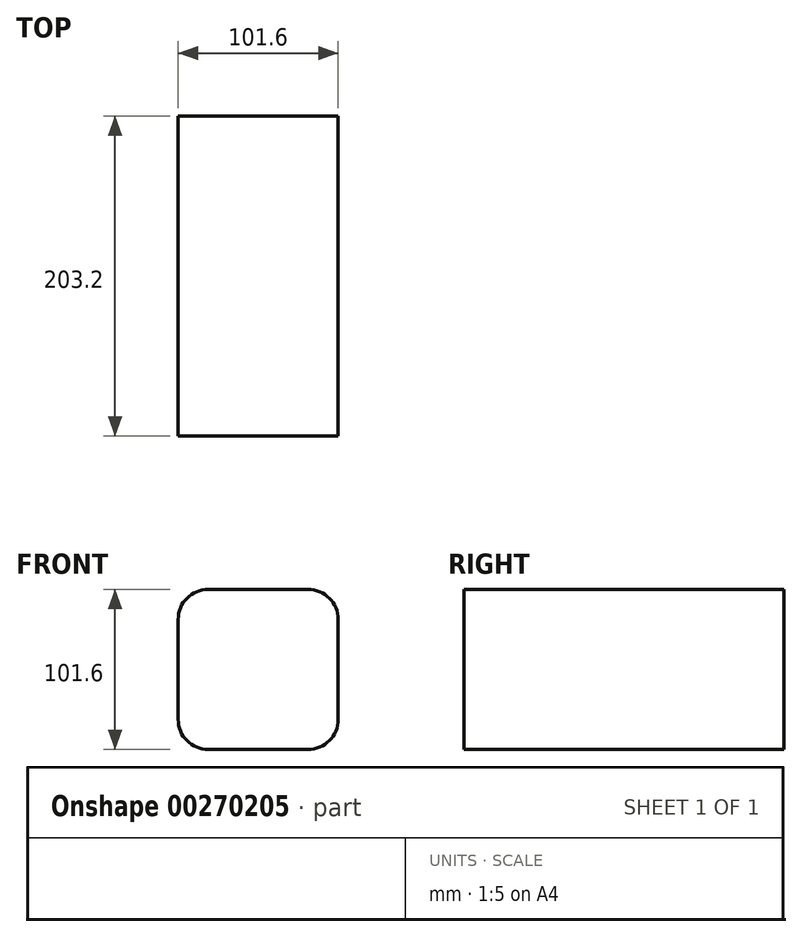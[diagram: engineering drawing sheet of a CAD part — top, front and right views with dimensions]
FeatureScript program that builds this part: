
annotation { "Feature Type Name" : "Feature", "Feature Type Description" : "" }
export const myFeature = defineFeature(function(context is Context, id is Id, definition is map)
    precondition{}
    {
        {
            var Q0;
            Q0=qCreatedBy(makeId("Front.planeOp"),FACE);
            var sketch = newSketch(context, id + "F0", { "sketchPlane" : qUnion([Q0])});
            skLineSegment(sketch, "E0.bottom", {"start": v(50.8, 50.8) * mm, "end": v(-50.8, 50.8) * mm});
            skLineSegment(sketch, "E0.top", {"start": v(50.8, -50.8) * mm, "end": v(-50.8, -50.8) * mm});
            skLineSegment(sketch, "E0.left", {"start": v(50.8, 50.8) * mm, "end": v(50.8, -50.8) * mm});
            skLineSegment(sketch, "E0.right", {"start": v(-50.8, 50.8) * mm, "end": v(-50.8, -50.8) * mm});
            skPoint(sketch, "E0.middle", {"position": v(0, 0) * mm});
            skSolve(sketch);
        }
        {
            var Q0;
            Q0=makeQuery(id+"F0.imprint","IMPRINT",FACE,{"disambiguationData":[TD([[makeQuery(id+"F0.imprint","IMPRINT",EDGE,{"derivedFrom":sQuery(id+"F0.wireOp",EDGE,"E0.bottom")}),1.0]])]});
            extrude(context, id + "F1", {"entities" : qUnion([Q0]), "depth" : 101.6 * mm, "hasSecondDirection" : true, "secondDirectionOppositeDirection" : true, "secondDirectionDepth" : 101.6 * mm});
        }
        {
            var Q0;
            Q0=makeQuery(id+"F1.opExtrude","SWEPT_EDGE",EDGE,{"disambiguationData":[OSD([sQuery(id+"F0.wireOp",EDGE,"E0.bottom"),sQuery(id+"F0.wireOp",EDGE,"E0.right")])]});
            var Q1;
            Q1=makeQuery(id+"F1.opExtrude","SWEPT_EDGE",EDGE,{"disambiguationData":[OSD([sQuery(id+"F0.wireOp",EDGE,"E0.bottom"),sQuery(id+"F0.wireOp",EDGE,"E0.left")])]});
            var Q2;
            Q2=makeQuery(id+"F1.opExtrude","SWEPT_EDGE",EDGE,{"disambiguationData":[OSD([sQuery(id+"F0.wireOp",EDGE,"E0.top"),sQuery(id+"F0.wireOp",EDGE,"E0.left")])]});
            var Q3;
            Q3=makeQuery(id+"F1.opExtrude","SWEPT_EDGE",EDGE,{"disambiguationData":[OSD([sQuery(id+"F0.wireOp",EDGE,"E0.top"),sQuery(id+"F0.wireOp",EDGE,"E0.right")])]});
            fillet(context, id + "F2", {"entities" : qUnion([Q0, Q1, Q2, Q3]), "radius" : 19.05 * mm, "tangentPropagation" : true, "allowEdgeOverflow" : false});
        }
        {
            var Q0;
            Q0=makeQuery(id+"F1.opExtrude","SWEPT_FACE",FACE,{"disambiguationData":[OSD([sQuery(id+"F0.wireOp",EDGE,"E0.top")])]});
            var sketch = newSketch(context, id + "F3", { "sketchPlane" : qUnion([Q0])});
            skCircle(sketch, "E1", {"center": v(-22.5, 95.33) * mm, "radius": 2.74 * mm});
            skPoint(sketch, "E1.first.point", {"position": v(-20.28, 96.93) * mm});
            skPoint(sketch, "E1.second.point", {"position": v(-24.96, 96.54) * mm});
            skPoint(sketch, "E1.third.point", {"position": v(-23.01, 92.64) * mm});
            skSolve(sketch);
        }
        {
            var Q0;
            Q0=makeQuery(id+"F3.imprint","IMPRINT",FACE,{"disambiguationData":[TD([[makeQuery(id+"F3.imprint","IMPRINT",EDGE,{"derivedFrom":sQuery(id+"F3.wireOp",EDGE,"E1")}),1.0]])]});
            extrude(context, id + "F4", {"entities" : qUnion([Q0]), "operationType" : NewBodyOperationType.ADD, "oppositeDirection" : true, "depth" : 19.3 * mm});
        }
    });
